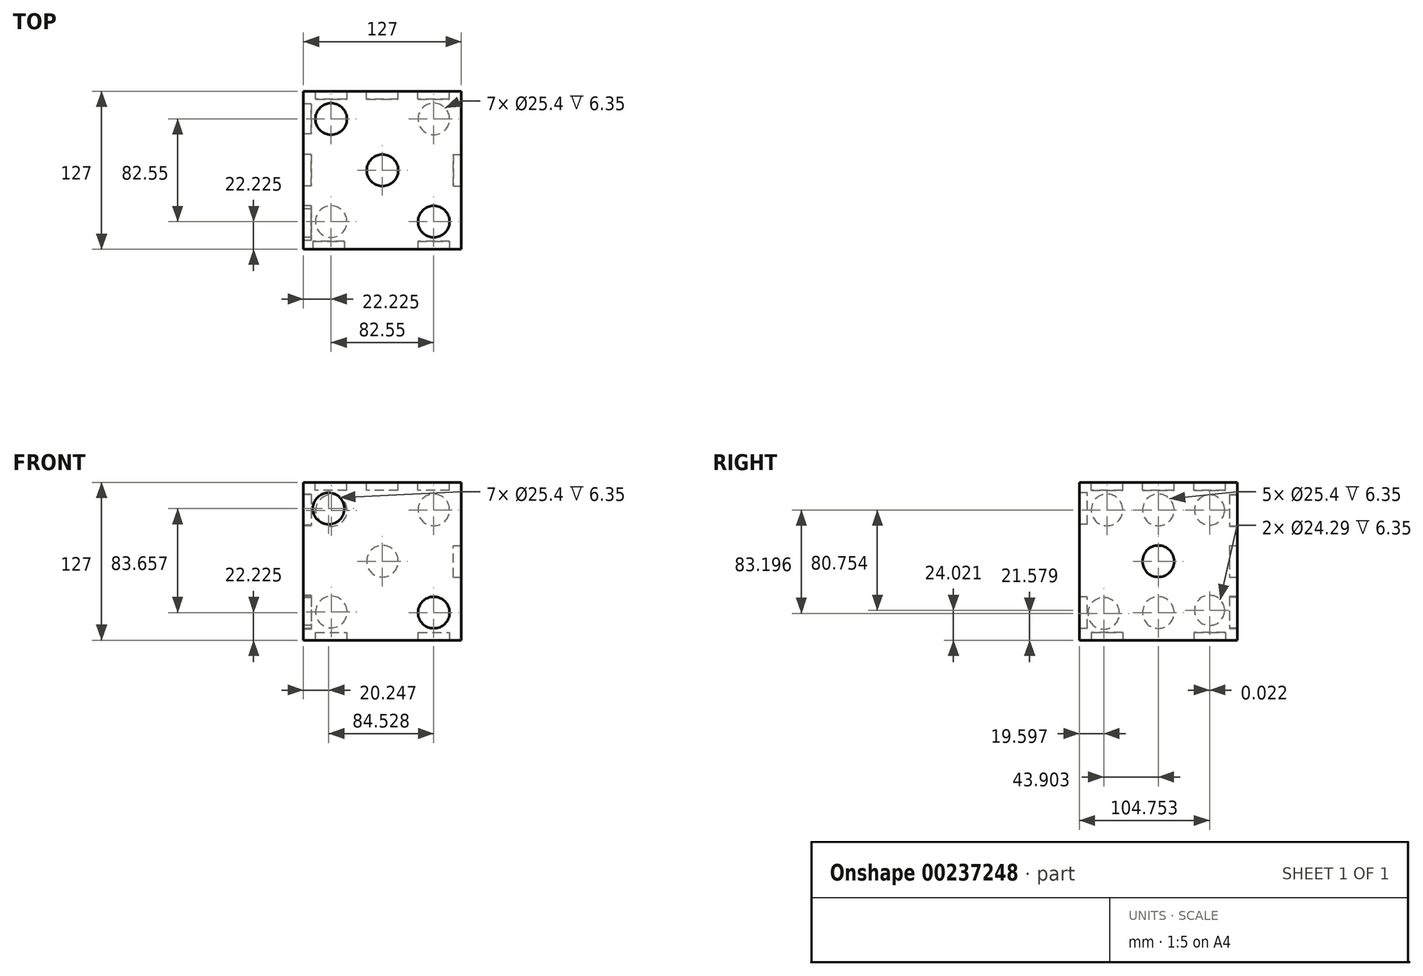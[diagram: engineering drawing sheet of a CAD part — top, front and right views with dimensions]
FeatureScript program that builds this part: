
annotation { "Feature Type Name" : "Feature", "Feature Type Description" : "" }
export const myFeature = defineFeature(function(context is Context, id is Id, definition is map)
    precondition{}
    {
        {
            var Q0;
            Q0=qCreatedBy(makeId("Top.planeOp"),FACE);
            var sketch = newSketch(context, id + "F0", { "sketchPlane" : qUnion([Q0])});
            skLineSegment(sketch, "E0.bottom", {"start": v(0, 0) * mm, "end": v(127, 0) * mm});
            skLineSegment(sketch, "E0.top", {"start": v(0, -127) * mm, "end": v(127, -127) * mm});
            skLineSegment(sketch, "E0.left", {"start": v(0, 0) * mm, "end": v(0, -127) * mm});
            skLineSegment(sketch, "E0.right", {"start": v(127, 0) * mm, "end": v(127, -127) * mm});
            skSolve(sketch);
        }
        {
            var Q0;
            Q0=makeQuery(id+"F0.imprint","IMPRINT",FACE,{"disambiguationData":[TD([[makeQuery(id+"F0.imprint","IMPRINT",EDGE,{"derivedFrom":sQuery(id+"F0.wireOp",EDGE,"E0.bottom")}),-1.0]])]});
            extrude(context, id + "F1", {"entities" : qUnion([Q0]), "depth" : 127 * mm});
        }
        {
            var Q0;
            Q0=makeQuery(id+"F1.opExtrude","SWEPT_FACE",FACE,{"disambiguationData":[OSD([sQuery(id+"F0.wireOp",EDGE,"E0.right")])]});
            var sketch = newSketch(context, id + "F2", { "sketchPlane" : qUnion([Q0])});
            skCircle(sketch, "E1", {"center": v(-63.5, 63.5) * mm, "radius": 12.7 * mm});
            skSolve(sketch);
        }
        {
            var Q0;
            Q0=makeQuery(id+"F2.imprint","IMPRINT",FACE,{"disambiguationData":[TD([[makeQuery(id+"F2.imprint","IMPRINT",EDGE,{"derivedFrom":sQuery(id+"F2.wireOp",EDGE,"E1")}),1.0]])]});
            extrude(context, id + "F3", {"entities" : qUnion([Q0]), "operationType" : NewBodyOperationType.REMOVE, "oppositeDirection" : true, "depth" : 6.35 * mm});
        }
        {
            var Q0;
            Q0=makeQuery(id+"F1.opExtrude","SWEPT_FACE",FACE,{"disambiguationData":[OSD([sQuery(id+"F0.wireOp",EDGE,"E0.top")])]});
            var sketch = newSketch(context, id + "F4", { "sketchPlane" : qUnion([Q0])});
            skCircle(sketch, "E2", {"center": v(104.78, 22.22) * mm, "radius": 12.7 * mm});
            skCircle(sketch, "E3", {"center": v(20.25, 105.88) * mm, "radius": 12.7 * mm});
            skSolve(sketch);
        }
        {
            var Q0;
            Q0=makeQuery(id+"F4.imprint","IMPRINT",FACE,{"disambiguationData":[TD([[makeQuery(id+"F4.imprint","IMPRINT",EDGE,{"derivedFrom":sQuery(id+"F4.wireOp",EDGE,"E3")}),1.0]])]});
            var Q1;
            Q1=makeQuery(id+"F4.imprint","IMPRINT",FACE,{"disambiguationData":[TD([[makeQuery(id+"F4.imprint","IMPRINT",EDGE,{"derivedFrom":sQuery(id+"F4.wireOp",EDGE,"E2")}),1.0]])]});
            extrude(context, id + "F5", {"entities" : qUnion([Q0, Q1]), "operationType" : NewBodyOperationType.REMOVE, "oppositeDirection" : true, "depth" : 6.35 * mm});
        }
        {
            var Q0;
            Q0=makeQuery(id+"F1.opExtrude","SWEPT_FACE",FACE,{"disambiguationData":[OSD([sQuery(id+"F0.wireOp",EDGE,"E0.left")])]});
            var sketch = newSketch(context, id + "F6", { "sketchPlane" : qUnion([Q0])});
            skCircle(sketch, "E4", {"center": v(63.5, 22.23) * mm, "radius": 12.7 * mm});
            skCircle(sketch, "E5", {"center": v(107.4, 21.58) * mm, "radius": 12.7 * mm});
            skSolve(sketch);
        }
        {
            var Q0;
            Q0=makeQuery(id+"F6.imprint","IMPRINT",FACE,{"disambiguationData":[TD([[makeQuery(id+"F6.imprint","IMPRINT",EDGE,{"derivedFrom":sQuery(id+"F6.wireOp",EDGE,"E4")}),1.0]])]});
            var sketch = newSketch(context, id + "F7", { "sketchPlane" : qUnion([Q0])});
            skCircle(sketch, "E6", {"center": v(22.25, 24.02) * mm, "radius": 12.15 * mm});
            skCircle(sketch, "E7", {"center": v(22.23, 104.78) * mm, "radius": 12.15 * mm});
            skCircle(sketch, "E8", {"center": v(63.5, 104.78) * mm, "radius": 12.7 * mm});
            skCircle(sketch, "E9", {"center": v(104.78, 104.78) * mm, "radius": 12.7 * mm});
            skSolve(sketch);
        }
        {
            var Q0;
            Q0=makeQuery(id+"F6.imprint","IMPRINT",FACE,{"disambiguationData":[TD([[makeQuery(id+"F6.imprint","IMPRINT",EDGE,{"derivedFrom":sQuery(id+"F6.wireOp",EDGE,"E5")}),1.0]])]});
            var Q1;
            Q1=makeQuery(id+"F7.imprint","IMPRINT",FACE,{"disambiguationData":[TD([[makeQuery(id+"F7.imprint","IMPRINT",EDGE,{"derivedFrom":makeQuery(id+"F6.imprint","IMPRINT",EDGE,{"derivedFrom":sQuery(id+"F6.wireOp",EDGE,"E4")})}),1.0]])]});
            var Q2;
            Q2=makeQuery(id+"F7.imprint","IMPRINT",FACE,{"disambiguationData":[TD([[makeQuery(id+"F7.imprint","IMPRINT",EDGE,{"derivedFrom":sQuery(id+"F7.wireOp",EDGE,"E6")}),1.0]])]});
            var Q3;
            Q3=makeQuery(id+"F7.imprint","IMPRINT",FACE,{"disambiguationData":[TD([[makeQuery(id+"F7.imprint","IMPRINT",EDGE,{"derivedFrom":sQuery(id+"F7.wireOp",EDGE,"E9")}),1.0]])]});
            var Q4;
            Q4=makeQuery(id+"F7.imprint","IMPRINT",FACE,{"disambiguationData":[TD([[makeQuery(id+"F7.imprint","IMPRINT",EDGE,{"derivedFrom":sQuery(id+"F7.wireOp",EDGE,"E8")}),1.0]])]});
            var Q5;
            Q5=makeQuery(id+"F7.imprint","IMPRINT",FACE,{"disambiguationData":[TD([[makeQuery(id+"F7.imprint","IMPRINT",EDGE,{"derivedFrom":sQuery(id+"F7.wireOp",EDGE,"E7")}),1.0]])]});
            extrude(context, id + "F8", {"entities" : qUnion([Q0, Q1, Q2, Q3, Q4, Q5]), "operationType" : NewBodyOperationType.REMOVE, "oppositeDirection" : true, "depth" : 6.35 * mm});
        }
        {
            var Q0;
            Q0=makeQuery(id+"F1.opExtrude","SWEPT_FACE",FACE,{"disambiguationData":[OSD([sQuery(id+"F0.wireOp",EDGE,"E0.bottom")])]});
            var sketch = newSketch(context, id + "F9", { "sketchPlane" : qUnion([Q0])});
            skCircle(sketch, "E10", {"center": v(-22.44, 104.35) * mm, "radius": 12.7 * mm});
            skCircle(sketch, "E11", {"center": v(-22.44, 22.65) * mm, "radius": 12.7 * mm});
            skCircle(sketch, "E12", {"center": v(-63.5, 63.5) * mm, "radius": 12.7 * mm});
            skCircle(sketch, "E13", {"center": v(-104.78, 104.78) * mm, "radius": 12.7 * mm});
            skCircle(sketch, "E14", {"center": v(-104.78, 22.22) * mm, "radius": 12.7 * mm});
            skSolve(sketch);
        }
        {
            var Q0;
            Q0=makeQuery(id+"F9.imprint","IMPRINT",FACE,{"disambiguationData":[TD([[makeQuery(id+"F9.imprint","IMPRINT",EDGE,{"derivedFrom":sQuery(id+"F9.wireOp",EDGE,"E10")}),1.0]])]});
            var Q1;
            Q1=makeQuery(id+"F9.imprint","IMPRINT",FACE,{"disambiguationData":[TD([[makeQuery(id+"F9.imprint","IMPRINT",EDGE,{"derivedFrom":sQuery(id+"F9.wireOp",EDGE,"E12")}),1.0]])]});
            var Q2;
            Q2=makeQuery(id+"F9.imprint","IMPRINT",FACE,{"disambiguationData":[TD([[makeQuery(id+"F9.imprint","IMPRINT",EDGE,{"derivedFrom":sQuery(id+"F9.wireOp",EDGE,"E11")}),1.0]])]});
            var Q3;
            Q3=makeQuery(id+"F9.imprint","IMPRINT",FACE,{"disambiguationData":[TD([[makeQuery(id+"F9.imprint","IMPRINT",EDGE,{"derivedFrom":sQuery(id+"F9.wireOp",EDGE,"E14")}),1.0]])]});
            var Q4;
            Q4=makeQuery(id+"F9.imprint","IMPRINT",FACE,{"disambiguationData":[TD([[makeQuery(id+"F9.imprint","IMPRINT",EDGE,{"derivedFrom":sQuery(id+"F9.wireOp",EDGE,"E13")}),1.0]])]});
            extrude(context, id + "F10", {"entities" : qUnion([Q0, Q1, Q2, Q3, Q4]), "operationType" : NewBodyOperationType.REMOVE, "oppositeDirection" : true, "depth" : 6.35 * mm});
        }
        {
            var Q0;
            Q0=makeQuery(id+"F1.opExtrude","CAP_FACE",FACE,{"disambiguationData":[OSD([sQuery(id+"F0.wireOp",EDGE,"E0.bottom"),sQuery(id+"F0.wireOp",EDGE,"E0.top"),sQuery(id+"F0.wireOp",EDGE,"E0.left"),sQuery(id+"F0.wireOp",EDGE,"E0.right")])],"isStart":true});
            var sketch = newSketch(context, id + "F11", { "sketchPlane" : qUnion([Q0])});
            skCircle(sketch, "E15", {"center": v(104.78, 104.78) * mm, "radius": 12.7 * mm});
            skCircle(sketch, "E16", {"center": v(104.78, 22.23) * mm, "radius": 12.7 * mm});
            skCircle(sketch, "E17", {"center": v(22.23, 104.78) * mm, "radius": 12.7 * mm});
            skCircle(sketch, "E18", {"center": v(22.23, 22.23) * mm, "radius": 12.7 * mm});
            skSolve(sketch);
        }
        {
            var Q0;
            Q0=makeQuery(id+"F11.imprint","IMPRINT",FACE,{"disambiguationData":[TD([[makeQuery(id+"F11.imprint","IMPRINT",EDGE,{"derivedFrom":sQuery(id+"F11.wireOp",EDGE,"E15")}),1.0]])]});
            var Q1;
            Q1=makeQuery(id+"F11.imprint","IMPRINT",FACE,{"disambiguationData":[TD([[makeQuery(id+"F11.imprint","IMPRINT",EDGE,{"derivedFrom":sQuery(id+"F11.wireOp",EDGE,"E17")}),1.0]])]});
            var Q2;
            Q2=makeQuery(id+"F11.imprint","IMPRINT",FACE,{"disambiguationData":[TD([[makeQuery(id+"F11.imprint","IMPRINT",EDGE,{"derivedFrom":sQuery(id+"F11.wireOp",EDGE,"E16")}),1.0]])]});
            var Q3;
            Q3=makeQuery(id+"F11.imprint","IMPRINT",FACE,{"disambiguationData":[TD([[makeQuery(id+"F11.imprint","IMPRINT",EDGE,{"derivedFrom":sQuery(id+"F11.wireOp",EDGE,"E18")}),1.0]])]});
            extrude(context, id + "F12", {"entities" : qUnion([Q0, Q1, Q2, Q3]), "operationType" : NewBodyOperationType.REMOVE, "oppositeDirection" : true, "depth" : 6.35 * mm});
        }
        {
            var Q0;
            Q0=makeQuery(id+"F1.opExtrude","CAP_FACE",FACE,{"disambiguationData":[OSD([sQuery(id+"F0.wireOp",EDGE,"E0.bottom"),sQuery(id+"F0.wireOp",EDGE,"E0.top"),sQuery(id+"F0.wireOp",EDGE,"E0.left"),sQuery(id+"F0.wireOp",EDGE,"E0.right")])],"isStart":false});
            var sketch = newSketch(context, id + "F13", { "sketchPlane" : qUnion([Q0])});
            skCircle(sketch, "E19", {"center": v(104.78, -104.78) * mm, "radius": 12.7 * mm});
            skCircle(sketch, "E20", {"center": v(22.23, -22.23) * mm, "radius": 12.7 * mm});
            skCircle(sketch, "E21", {"center": v(63.5, -63.5) * mm, "radius": 12.7 * mm});
            skSolve(sketch);
        }
        {
            var Q0;
            Q0=makeQuery(id+"F13.imprint","IMPRINT",FACE,{"disambiguationData":[TD([[makeQuery(id+"F13.imprint","IMPRINT",EDGE,{"derivedFrom":sQuery(id+"F13.wireOp",EDGE,"E21")}),1.0]])]});
            var Q1;
            Q1=makeQuery(id+"F13.imprint","IMPRINT",FACE,{"disambiguationData":[TD([[makeQuery(id+"F13.imprint","IMPRINT",EDGE,{"derivedFrom":sQuery(id+"F13.wireOp",EDGE,"E19")}),1.0]])]});
            var Q2;
            Q2=makeQuery(id+"F13.imprint","IMPRINT",FACE,{"disambiguationData":[TD([[makeQuery(id+"F13.imprint","IMPRINT",EDGE,{"derivedFrom":sQuery(id+"F13.wireOp",EDGE,"E20")}),1.0]])]});
            extrude(context, id + "F14", {"entities" : qUnion([Q0, Q1, Q2]), "operationType" : NewBodyOperationType.REMOVE, "oppositeDirection" : true, "depth" : 6.35 * mm});
        }
    });
